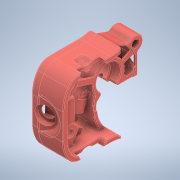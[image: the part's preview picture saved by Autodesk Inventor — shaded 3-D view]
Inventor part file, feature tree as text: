
AUTODESK INVENTOR PART (.ipt)
format: ipt  version: 2021 (Build 250183000, 183)  size: 4,622,848 bytes
history: native  units: mm
features: sketch x57, extrude x50, projected_geometry x22, fillet x20, plane x11, sweep x6, chamfer x6, mirror x4, other x3, revolve x2
ambient origin geometry x8: Origin, YZ Plane, XZ Plane, XY Plane, X Axis, Y Axis, Z Axis, Center Point
bodies: Body1 (feature_tree)
feature tree (181):
  parser-record x1  (decoder bookkeeping rows leaked as tree rows — omitted from the tree; the rows remain in map.json)
  other  "Sólido1"
  extrude  "Extrusión1"  Depth=1.0mm
  extrude  "Extrusión2"  Depth=1.0mm
  extrude  "Extrusión3"  Depth=6.5mm
  sketch  "Boceto3"  dims[d6=6.5mm d8=6.5mm]
  sketch  "Boceto7"  dims[d26=0.5mm d27=6.0mm]
  sweep  "Barrido4"
  sweep  "Barrido5"
  extrude  "Extrusión4"  TaperAngle=0.0deg  [1 undecoded]
  revolve  "Revolución5"  [1 undecoded]
  revolve  "Revolución6"  [1 undecoded]
  extrude  "Extrusión6"  Depth=1.0mm
  fillet  "Empalme1"  Radius=10.5mm
  fillet  "Empalme2"  Radius=1.0mm
  fillet  "Empalme3"  Radius=31.5mm
  fillet  "Empalme4"  Radius=4.0mm
  extrude  "Extrusión7"  Depth=4.0mm
  extrude  "Extrusión8"  Depth=0.5mm
  extrude  "Extrusión12"  Depth=0.25mm
  extrude  "Extrusión13"  Depth=5.0mm TaperAngle=0.0deg
  extrude  "Extrusión14"  Depth=7.0mm
  plane  "Plano de trabajo4"
  extrude  "Extrusión15"  Depth=10.0mm TaperAngle=0.0deg
  plane  "Plano de trabajo5"
  sketch  "Boceto35"  dims[d78=2.9mm d79=5.2mm]
  sketch  "Boceto36"  dims[d80=1.2mm d89=0.8mm]
  sweep  "Barrido6"
  extrude  "Extrusión16"  Depth=0.8mm
  sweep  "Barrido7"
  extrude  "Extrusión17"  Depth=1.0mm
  extrude  "Extrusión18"  Depth=52.0mm
  fillet  "Empalme7"  Radius=2.0mm
  fillet  "Empalme8"  Radius=5.0mm
  fillet  "Empalme9"  Radius=7.0mm
  fillet  "Empalme10"  Radius=4.5mm
  fillet  "Empalme11"  Radius=6.0mm
  extrude  "Extrusión19"  Depth=1.0mm
  extrude  "Extrusión20"  TaperAngle=0.0deg  [1 undecoded]
  extrude  "Extrusión21"  Depth=6.5mm
  extrude  "Extrusión22"  Depth=10.0mm TaperAngle=0.0deg
  extrude  "Extrusión23"  Depth=5.5mm
  extrude  "Extrusión24"  Depth=0.5mm
  plane  "Plano de trabajo6"
  plane  "Plano de trabajo7"
  mirror  "Simetría1"
  mirror  "Simetría2"
  extrude  "Extrusión25"  Depth=2.0mm
  plane  "Plano de trabajo8"
  plane  "Plano de trabajo9"
  mirror  "Simetría3"
  mirror  "Simetría4"
  extrude  "Extrusión26"  Depth=1.0mm
  fillet  "Empalme13"  Radius=1.0mm
  extrude  "Extrusión27"  Depth=0.3mm
  extrude  "Extrusión28"  Depth=7.0mm
  extrude  "Extrusión29"  Depth=1.0mm
  extrude  "Extrusión30"  Depth=1.2mm
  fillet  "Empalme14"  Radius=5.2mm
  fillet  "Empalme15"  Radius=6.0mm
  fillet  "Empalme16"  Radius=5.95mm
  extrude  "Extrusión31"  Depth=7.2mm TaperAngle=0.0deg
  extrude  "Extrusión32"  Depth=5.95mm
  extrude  "Extrusión33"  Depth=0.8mm TaperAngle=0.0deg
  extrude  "Extrusión34"  Depth=0.8mm
  fillet  "Empalme17"  Radius=1.2mm
  chamfer  "Chaflán1"  Distance=1.2mm
  plane  "Plano de trabajo13"
  extrude  "Extrusión49"  Depth=1.0mm
  extrude  "Extrusión50"  Depth=10.0mm TaperAngle=0.0deg
  sketch  "Boceto77"  dims[d173=1.2mm d174=0.0mm d175=1.0mm]
  plane  "Plano de trabajo14"
  extrude  "Extrusión51"  Depth=10.0mm TaperAngle=0.0deg
  sketch  "Boceto79"  dims[d180=1.7mm d181=10.0mm d182=0.0mm]
  plane  "Plano de trabajo15"
  extrude  "Extrusión54"  Depth=1.0mm
  sweep  "Barrido10"
  sweep  "Barrido11"
  extrude  "Extrusión52"  Depth=1.0mm
  extrude  "Extrusión53"  Depth=1.45mm
  sketch  "Boceto84"  dims[d196=0.3mm d197=1.0mm]
  extrude  "Extrusión55"  Depth=2.6mm
  extrude  "Extrusión56"  Depth=1.0mm
  fillet  "Empalme21"  Radius=1.0mm
  extrude  "Extrusión57"  Depth=1.0mm TaperAngle=0.0deg
  fillet  "Empalme25"  Radius=7.5mm
  chamfer  "Chaflán3"  Distance=4.0mm
  plane  "Plano de trabajo17"
  extrude  "Extrusión59"  Depth=5.0mm TaperAngle=0.0deg
  extrude  "Extrusión62"  Depth=3.0mm
  extrude  "Extrusión63"  [1 undecoded]
  plane  "Plano de trabajo18"
  extrude  "Extrusión65"  Depth=18.0mm
  extrude  "Extrusión68"  Depth=10.0mm TaperAngle=0.0deg
  extrude  "Extrusión69"  Depth=10.0mm TaperAngle=0.0deg
  chamfer  "Chaflán6"  Angle=75.0deg  [1 undecoded]
  fillet  "Empalme28"  Radius=5.0mm
  fillet  "Empalme29"  Radius=4.0mm
  fillet  "Empalme30"  Radius=3.0mm
  chamfer  "Chaflán8"  Distance=10.449868mm
  chamfer  "Chaflán10"  Distance=8.5mm
  chamfer  "Chaflán11"  Distance=8.5mm
  extrude  "Extrusión67"  Depth=1.0mm TaperAngle=0.0deg
  fillet  "Empalme34"  [1 undecoded]
  extrude  "Extrusión74"  TaperAngle=0.0deg  [1 undecoded]
  extrude  "Extrusión75"  Depth=1.0mm
  extrude  "Extrusión76"  Depth=1.0mm TaperAngle=0.0deg
  extrude  "Extrusión77"  Depth=1.0mm
  sketch  "Boceto1"  dims[d0=0.6mm d1=0.0mm d2=1.0mm]
  projected_geometry  "Contorno proyectado1"
  sketch  "Boceto2"  dims[d3=1.0mm d4=0.0mm d5=4.5mm]
  sketch  "Boceto6"  dims[d15=2.0mm d16=9.7mm d17=0.0mm]
  sketch  "Boceto8"  dims[d28=0.0mm d29=0.0mm d30=0.0mm d31=0.0mm]
  sketch  "Boceto15"  dims[d32=2.0mm d33=10.0mm d34=0.0mm]
  sketch  "Boceto16"  dims[d52=1.0mm d53=4.5mm]
  sketch  "Boceto18"  dims[d54=90.0deg d55=1.4mm d56=10.5mm d57=1.0mm d58=31.5mm d59=4.0mm]
  sketch  "Boceto19"  dims[d60=5.5mm d62=4.0mm]
  sketch  "Boceto22"  dims[d63=3.0mm d64=0.0mm d65=0.5mm]
  sketch  "Boceto27"  dims[d66=0.5mm d67=0.25mm]
  sketch  "Boceto28"  dims[d68=5.5mm d69=5.0mm d70=0.0mm]
  projected_geometry  "Contorno proyectado3"
  sketch  "Boceto29"  dims[d73=5.0mm d74=7.0mm]
  projected_geometry  "Contorno proyectado4"
  sketch  "Boceto30"  dims[d75=1.0mm d76=10.0mm d77=0.0mm]
  sketch  "Boceto37"  dims[d90=5.95mm d91=0.0mm]
  sketch  "Boceto38"  dims[d92=0.8mm d93=0.0mm d94=1.0mm]
  projected_geometry  "Contorno proyectado5"
  sketch  "Boceto39"  dims[d96=7.2mm d97=0.0mm d98=52.0mm d99=2.0mm d100=5.0mm d101=7.0mm d102=0.0mm d108=4.5mm d109=6.0mm]
  sketch  "Boceto40"  dims[d110=1.0mm d111=28.0mm]
  sketch  "Boceto41"  dims[d112=6.5mm d113=0.0mm d114=0.0mm]
  sketch  "Boceto42"  dims[d115=5.0mm d116=6.5mm]
  projected_geometry  "Contorno proyectado6"
  sketch  "Boceto43"  dims[d117=2.0mm d118=10.0mm d119=0.0mm]
  sketch  "Boceto44"  dims[d120=0.0mm d121=0.0mm d122=5.5mm]
  projected_geometry  "Contorno proyectado7"
  sketch  "Boceto45"  dims[d123=5.5mm d124=0.0mm d125=0.5mm]
  sketch  "Boceto47"  dims[d127=0.5mm d128=2.0mm]
  sketch  "Boceto48"  dims[d129=6.0mm d130=0.0mm d131=1.0mm d132=1.0mm]
  projected_geometry  "Contorno proyectado8"
  projected_geometry  "Contorno proyectado9"
  projected_geometry  "Contorno proyectado10"
  sketch  "Boceto50"  dims[d133=0.3mm d134=0.3mm]
  projected_geometry  "Contorno proyectado12"
  projected_geometry  "Contorno proyectado13"
  sketch  "Boceto51"  dims[d135=0.5mm d138=7.0mm]
  projected_geometry  "Contorno proyectado14"
  sketch  "Boceto52"  dims[d140=5.0mm d141=1.0mm]
  sketch  "Boceto53"  dims[d145=2.9mm d146=1.2mm d147=5.2mm d148=6.0mm d149=0.0mm d150=5.95mm]
  projected_geometry  "Contorno proyectado15"
  sketch  "Boceto55"  dims[d151=0.0mm d152=7.2mm d153=0.0mm]
  projected_geometry  "Contorno proyectado16"
  sketch  "Boceto58"  dims[d154=0.8mm d155=5.95mm]
  sketch  "Boceto59"  dims[d156=0.0mm d157=0.8mm d158=0.0mm]
  sketch  "Boceto61"  dims[d161=0.5mm d162=0.8mm d163=1.2mm d164=0.0mm]
  sketch  "Boceto74"  dims[d169=0.5mm]
  projected_geometry  "Contorno proyectado24"
  projected_geometry  "Contorno proyectado25"
  projected_geometry  "Contorno proyectado26"
  projected_geometry  "Contorno proyectado27"
  projected_geometry  "Contorno proyectado28"
  sketch  "Boceto75"  dims[d170=0.8mm d171=1.2mm d172=0.0mm]
  projected_geometry  "Contorno proyectado29"
  sketch  "Boceto78"  dims[d177=1.7mm d178=10.0mm d179=0.0mm]
  projected_geometry  "Contorno proyectado30"
  sketch  "Boceto81"  dims[d184=1.0mm d185=0.0mm d190=2.0mm]
  sketch  "Boceto82"  dims[d191=1.0mm d192=31.4mm]
  sketch  "Boceto83"  dims[d193=1.0mm d194=0.0mm d195=0.5mm]
  sketch  "Boceto85"  dims[d198=5.2mm d199=1.45mm]
  sketch  "Boceto89"  dims[d200=2.9mm d201=2.6mm]
  sketch  "Boceto92"  dims[d202=13.589024mm d203=30.0mm d204=1.0mm]
  sketch  "Boceto93"  dims[d206=1.0mm d207=0.6mm d208=0.0mm d210=7.5mm d211=4.0mm d212=0.0mm]
  sketch  "Boceto94"  dims[d213=7.5mm d214=5.0mm d215=0.0mm]
  sketch  "Boceto96"  dims[d217=3.0mm d218=0.0mm d219=3.0mm]
  sketch  "Boceto97"  dims[d221=0.4mm d222=2.0mm d223=45.0deg d273=-14.0mm]
  sketch  "Boceto98"  dims[d276=50.0mm d277=0.0mm d278=18.0mm]
  sketch  "Boceto104"  dims[d279=12.0mm d280=10.0mm d281=0.0mm]
  projected_geometry  "Contorno proyectado31"
  sketch  "Boceto105"  dims[d282=2.1595mm d283=10.0mm d284=0.0mm]
  sketch  "Boceto106"  dims[d285=165.0deg]
  sketch  "Boceto107"  dims[d287=5.0mm d288=75.0deg d293=5.0mm d294=0.0mm d295=4.0mm d296=3.0mm d297=0.0mm d298=10.449868mm d299=8.5mm d300=8.5mm d301=8.0mm d302=0.0mm d303=0.0mm d304=0.0mm d305=0.0mm d306=0.0mm d307=8.8mm d308=4.75mm d309=0.0mm d310=8.5mm d311=2.25mm d312=0.0mm d314=3.0mm d316=2.25mm d317=0.0mm d319=0.5mm d328=10.449868mm d333=2.0mm d334=0.4mm d335=2.0mm d336=45.0deg d337=9.4mm d338=10.0mm d339=0.0mm d347=-2.7mm d348=5.4mm d349=0.0mm d350=6.2mm d351=5.5mm d352=0.0mm d353=-0.4mm d354=10.0mm d357=5.2mm d358=0.0mm d361=0.0mm d362=0.0mm d364=1.0mm d365=0.0mm d368=11.5mm d369=0.5mm d370=0.5mm d371=0.4mm d372=1.0mm d376=4.0mm d377=0.0mm d383=0.5mm d384=2.0mm d385=45.0deg d386=1.0mm d387=1.0mm d391=0.5mm d392=2.0mm d393=2.0mm d394=45.0deg d398=3.0mm d399=5.0mm d400=45.0deg d401=3.0mm d402=5.0mm d403=45.0deg d421=0.5mm d422=6.5mm d423=5.5mm d424=0.0mm d425=5.5mm d426=0.0mm d427=6.5mm d428=5.5mm d429=0.0mm d430=7.0mm d431=0.0mm d432=7.6mm d433=7.6mm d40=50.0mm d41=50.0mm]
  other  "[a]_Mid_Body_x1"
note: 8 required parameter values undecoded (feature->parameter linkage not recoverable at this tier; creation-order binding heuristic only, values carry confidence <= 0.55)
note: 1 file-system path scrubbed to <path> (originals preserved in map.json)